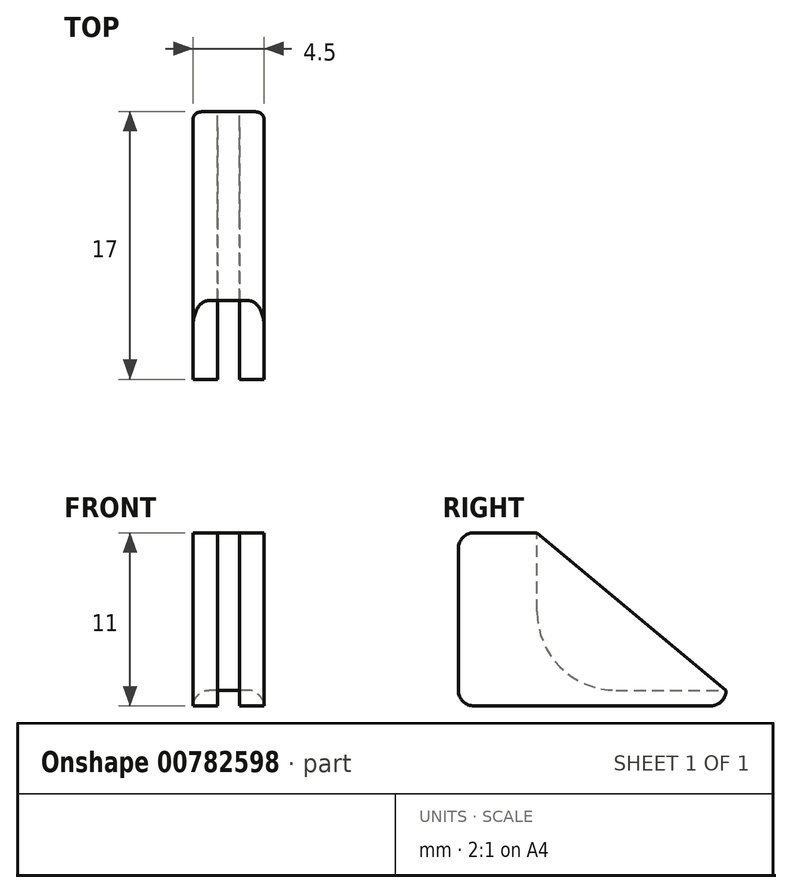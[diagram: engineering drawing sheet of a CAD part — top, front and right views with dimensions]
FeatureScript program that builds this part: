
annotation { "Feature Type Name" : "Feature", "Feature Type Description" : "" }
export const myFeature = defineFeature(function(context is Context, id is Id, definition is map)
    precondition{}
    {
        {
            var Q0;
            Q0=qCreatedBy(makeId("Right.planeOp"),FACE);
            var sketch = newSketch(context, id + "F0", { "sketchPlane" : qUnion([Q0])});
            skLineSegment(sketch, "E0", {"start": v(0, 0) * mm, "end": v(0, 10) * mm});
            skLineSegment(sketch, "E1", {"start": v(0, 0) * mm, "end": v(12, 0) * mm});
            skLineSegment(sketch, "E2", {"start": v(12, 0) * mm, "end": v(0, 10) * mm});
            skLineSegment(sketch, "E3", {"start": v(0, 10) * mm, "end": v(-5, 10) * mm});
            skLineSegment(sketch, "E4", {"start": v(0, 0) * mm, "end": v(-5, 0) * mm});
            skLineSegment(sketch, "E5", {"start": v(-5, 0) * mm, "end": v(-5, 10) * mm});
            skLineSegment(sketch, "E6", {"start": v(12, 0) * mm, "end": v(12, -1) * mm});
            skLineSegment(sketch, "E7", {"start": v(12, -1) * mm, "end": v(-5, -1) * mm});
            skLineSegment(sketch, "E8", {"start": v(-5, -1) * mm, "end": v(-5, 0) * mm});
            skSolve(sketch);
        }
        {
            var Q0;
            Q0 = qSketchRegion(id + "F0", true);
            extrude(context, id + "F1", {"entities" : qUnion([Q0]), "depth" : 4.5 * mm, "offsetDistance" : 25 * mm});
        }
        {
            var Q0;
            Q0=makeQuery(id+"F1.opExtrude","SWEPT_FACE",FACE,{"disambiguationData":[OSD([sQuery(id+"F0.wireOp",EDGE,"E3")])]});
            var sketch = newSketch(context, id + "F2", { "sketchPlane" : qUnion([Q0])});
            skLineSegment(sketch, "E9.bottom", {"start": v(2.95, -5) * mm, "end": v(1.55, -5) * mm});
            skLineSegment(sketch, "E9.top", {"start": v(2.95, 0) * mm, "end": v(1.55, 0) * mm});
            skLineSegment(sketch, "E9.left", {"start": v(2.95, -5) * mm, "end": v(2.95, 0) * mm});
            skLineSegment(sketch, "E9.right", {"start": v(1.55, -5) * mm, "end": v(1.55, 0) * mm});
            skSolve(sketch);
        }
        {
            var Q0;
            Q0 = qSketchRegion(id + "F2", true);
            extrude(context, id + "F3", {"entities" : qUnion([Q0]), "operationType" : NewBodyOperationType.REMOVE, "oppositeDirection" : true, "depth" : 25 * mm, "offsetDistance" : 25 * mm});
        }
        {
            var Q0;
            Q0=makeQuery(id+"F1.opExtrude","SWEPT_FACE",FACE,{"disambiguationData":[OSD([sQuery(id+"F0.wireOp",EDGE,"E6")])]});
            var sketch = newSketch(context, id + "F4", { "sketchPlane" : qUnion([Q0])});
            skLineSegment(sketch, "E10.bottom", {"start": v(-2.95, 0) * mm, "end": v(-1.55, 0) * mm});
            skLineSegment(sketch, "E10.top", {"start": v(-2.95, -1) * mm, "end": v(-1.55, -1) * mm});
            skLineSegment(sketch, "E10.left", {"start": v(-2.95, 0) * mm, "end": v(-2.95, -1) * mm});
            skLineSegment(sketch, "E10.right", {"start": v(-1.55, 0) * mm, "end": v(-1.55, -1) * mm});
            skSolve(sketch);
        }
        {
            var Q0;
            Q0 = qSketchRegion(id + "F4", true);
            extrude(context, id + "F5", {"entities" : qUnion([Q0]), "operationType" : NewBodyOperationType.REMOVE, "oppositeDirection" : true, "depth" : 25 * mm, "offsetDistance" : 25 * mm});
        }
        {
            var Q0;
            {var subQ0=sQuery(id+"F0.wireOp",EDGE,"E7");var subQ1=sQuery(id+"F0.wireOp",EDGE,"E6");Q0=makeQuery(id+"F5.boolean.opBoolean","SPLIT",EDGE,{"disambiguationData":[TD([makeQuery(id+"F3.boolean.opBoolean","COPY",FACE,{"derivedFrom":makeQuery(id+"F3.opExtrude","SWEPT_FACE",FACE,{"disambiguationData":[OSD([sQuery(id+"F2.wireOp",EDGE,"E9.left")])]})})])],"derivedFrom":makeQuery(id+"F1.opExtrude","SWEPT_EDGE",EDGE,{"disambiguationData":[OSD([subQ1,subQ0])]})});}
            var Q1;
            {var subQ0=sQuery(id+"F0.wireOp",EDGE,"E6");var subQ1=sQuery(id+"F0.wireOp",EDGE,"E7");Q1=makeQuery(id+"F5.boolean.opBoolean","SPLIT",EDGE,{"disambiguationData":[TD([makeQuery(id+"F3.boolean.opBoolean","COPY",FACE,{"derivedFrom":makeQuery(id+"F3.opExtrude","SWEPT_FACE",FACE,{"disambiguationData":[OSD([sQuery(id+"F2.wireOp",EDGE,"E9.right")])]})})])],"derivedFrom":makeQuery(id+"F1.opExtrude","SWEPT_EDGE",EDGE,{"disambiguationData":[OSD([subQ0,subQ1])]})});}
            var Q2;
            {var subQ0=sQuery(id+"F0.wireOp",EDGE,"E8");var subQ1=sQuery(id+"F0.wireOp",EDGE,"E7");Q2=makeQuery(id+"F3.boolean.opBoolean","SPLIT",EDGE,{"disambiguationData":[TD([makeQuery(id+"F3.opExtrude","SWEPT_FACE",FACE,{"disambiguationData":[OSD([sQuery(id+"F2.wireOp",EDGE,"E9.left")])]})])],"derivedFrom":makeQuery(id+"F1.opExtrude","SWEPT_EDGE",EDGE,{"disambiguationData":[OSD([subQ1,subQ0])]})});}
            var Q3;
            {var subQ0=sQuery(id+"F0.wireOp",EDGE,"E8");var subQ1=sQuery(id+"F0.wireOp",EDGE,"E7");Q3=makeQuery(id+"F3.boolean.opBoolean","SPLIT",EDGE,{"disambiguationData":[TD([makeQuery(id+"F3.opExtrude","SWEPT_FACE",FACE,{"disambiguationData":[OSD([sQuery(id+"F2.wireOp",EDGE,"E9.right")])]})])],"derivedFrom":makeQuery(id+"F1.opExtrude","SWEPT_EDGE",EDGE,{"disambiguationData":[OSD([subQ1,subQ0])]})});}
            var Q4;
            {var subQ1=sQuery(id+"F0.wireOp",EDGE,"E5");var subQ2=sQuery(id+"F0.wireOp",EDGE,"E3");Q4=makeQuery(id+"F3.boolean.opBoolean","SPLIT",EDGE,{"disambiguationData":[TD([makeQuery(id+"F3.opExtrude","SWEPT_FACE",FACE,{"disambiguationData":[OSD([sQuery(id+"F2.wireOp",EDGE,"E9.right")])]})])],"derivedFrom":makeQuery(id+"F1.opExtrude","SWEPT_EDGE",EDGE,{"disambiguationData":[OSD([subQ2,subQ1])]})});}
            var Q5;
            {var subQ1=sQuery(id+"F0.wireOp",EDGE,"E5");var subQ2=sQuery(id+"F0.wireOp",EDGE,"E3");Q5=makeQuery(id+"F3.boolean.opBoolean","SPLIT",EDGE,{"disambiguationData":[TD([makeQuery(id+"F3.opExtrude","SWEPT_FACE",FACE,{"disambiguationData":[OSD([sQuery(id+"F2.wireOp",EDGE,"E9.left")])]})])],"derivedFrom":makeQuery(id+"F1.opExtrude","SWEPT_EDGE",EDGE,{"disambiguationData":[OSD([subQ2,subQ1])]})});}
            var Q6;
            Q6=makeQuery(id+"F1.opExtrude","CAP_EDGE",EDGE,{"disambiguationData":[OSD([sQuery(id+"F0.wireOp",EDGE,"E2")])],"isStart":true});
            var Q7;
            Q7=makeQuery(id+"F1.opExtrude","CAP_EDGE",EDGE,{"disambiguationData":[OSD([sQuery(id+"F0.wireOp",EDGE,"E2")])],"isStart":false});
            fillet(context, id + "F6", {"entities" : qUnion([Q0, Q1, Q2, Q3, Q4, Q5, Q6, Q7]), "radius" : 1 * mm, "tangentPropagation" : true, "allowEdgeOverflow" : false});
        }
        {
            var Q0;
            Q0=makeQuery(id+"F5.boolean.opBoolean","INTERSECT",EDGE,{"derivedFrom":[makeQuery(id+"F3.boolean.opBoolean","COPY",FACE,{"derivedFrom":makeQuery(id+"F3.opExtrude","SWEPT_FACE",FACE,{"disambiguationData":[OSD([sQuery(id+"F2.wireOp",EDGE,"E9.top")])]})}),makeQuery(id+"F5.opExtrude","SWEPT_FACE",FACE,{"disambiguationData":[OSD([sQuery(id+"F4.wireOp",EDGE,"E10.bottom")])]})]});
            fillet(context, id + "F7", {"entities" : qUnion([Q0]), "radius" : 5 * mm, "tangentPropagation" : true, "allowEdgeOverflow" : false});
        }
    });
